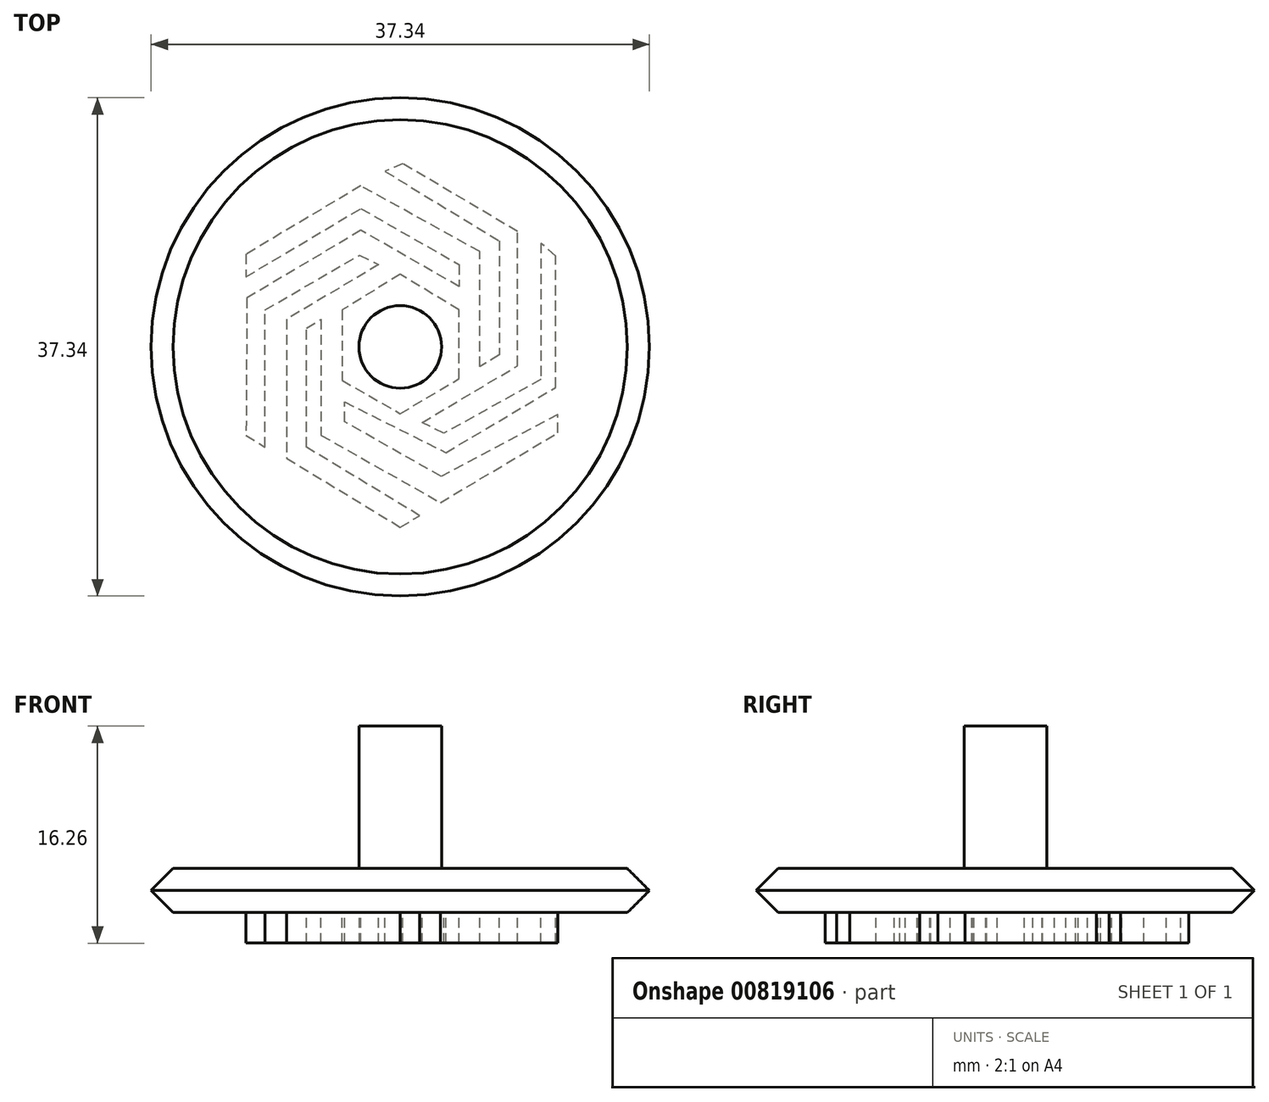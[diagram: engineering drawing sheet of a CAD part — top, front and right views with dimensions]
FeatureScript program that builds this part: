
annotation { "Feature Type Name" : "Feature", "Feature Type Description" : "" }
export const myFeature = defineFeature(function(context is Context, id is Id, definition is map)
    precondition{}
    {
        {
            var Q0;
            Q0=qCreatedBy(makeId("Top.planeOp"),FACE);
            var sketch = newSketch(context, id + "F0", { "sketchPlane" : qUnion([Q0])});
            skCircle(sketch, "E0", {"center": v(0, 0) * mm, "radius": 19.05 * mm});
            skSolve(sketch);
        }
        {
            var Q0;
            Q0=makeQuery(id+"F0.imprint","IMPRINT",FACE,{"disambiguationData":[TD([[makeQuery(id+"F0.imprint","IMPRINT",EDGE,{"derivedFrom":sQuery(id+"F0.wireOp",EDGE,"E0")}),1.0]])]});
            extrude(context, id + "F1", {"entities" : qUnion([Q0]), "depth" : 3.3 * mm, "offsetDistance" : 25.4 * mm});
        }
        {
            var Q0;
            Q0=makeQuery(id+"F1.opExtrude","CAP_FACE",FACE,{"disambiguationData":[OSD([sQuery(id+"F0.wireOp",EDGE,"E0")])],"isStart":false});
            var sketch = newSketch(context, id + "F2", { "sketchPlane" : qUnion([Q0])});
            skCircle(sketch, "E1", {"center": v(0, 0) * mm, "radius": 3.1 * mm});
            skSolve(sketch);
        }
        {
            var Q0;
            Q0=makeQuery(id+"F2.imprint","IMPRINT",FACE,{"disambiguationData":[TD([[makeQuery(id+"F2.imprint","IMPRINT",EDGE,{"derivedFrom":sQuery(id+"F2.wireOp",EDGE,"E1")}),1.0]])]});
            extrude(context, id + "F3", {"entities" : qUnion([Q0]), "operationType" : NewBodyOperationType.ADD, "depth" : 10.67 * mm, "offsetDistance" : 25.4 * mm});
        }
        {
            var Q0;
            Q0=makeQuery(id+"F1.opExtrude","CAP_EDGE",EDGE,{"disambiguationData":[OSD([sQuery(id+"F0.wireOp",EDGE,"E0")])],"isStart":false});
            chamfer(context, id + "F4", {"entities" : qUnion([Q0]), "width" : 2.03 * mm, "tangentPropagation" : true});
        }
        {
            var Q0;
            Q0=makeQuery(id+"F1.opExtrude","CAP_EDGE",EDGE,{"disambiguationData":[OSD([sQuery(id+"F0.wireOp",EDGE,"E0")])],"isStart":true});
            chamfer(context, id + "F5", {"entities" : qUnion([Q0]), "width" : 2.03 * mm, "tangentPropagation" : true});
        }
        {
            var Q0;
            Q0=makeQuery(id+"F1.opExtrude","CAP_FACE",FACE,{"disambiguationData":[OSD([sQuery(id+"F0.wireOp",EDGE,"E0")])],"isStart":true});
            var sketch = newSketch(context, id + "F6", { "sketchPlane" : qUnion([Q0])});
            skLineSegment(sketch, "E2", {"start": v(-11.55, 6.62) * mm, "end": v(-10.12, 7.5) * mm});
            skLineSegment(sketch, "E3", {"start": v(-10.12, 7.5) * mm, "end": v(-10.12, -2.78) * mm});
            skLineSegment(sketch, "E4", {"start": v(-10.12, -2.78) * mm, "end": v(-3.05, -6.88) * mm});
            skLineSegment(sketch, "E5", {"start": v(-3.05, -6.88) * mm, "end": v(-1.62, -6.16) * mm});
            skLineSegment(sketch, "E6", {"start": v(-1.62, -6.16) * mm, "end": v(-8.52, -2.06) * mm});
            skLineSegment(sketch, "E7", {"start": v(-8.52, -2.06) * mm, "end": v(-8.52, 8.34) * mm});
            skLineSegment(sketch, "E8", {"start": v(-8.52, 8.34) * mm, "end": v(0, 13.5) * mm});
            skLineSegment(sketch, "E9", {"start": v(0, 13.5) * mm, "end": v(1.45, 12.65) * mm});
            skLineSegment(sketch, "E10", {"start": v(1.45, 12.65) * mm, "end": v(-7.03, 7.5) * mm});
            skLineSegment(sketch, "E11", {"start": v(-7.03, 7.5) * mm, "end": v(-7.03, -1.4) * mm});
            skLineSegment(sketch, "E12", {"start": v(-7.03, -1.4) * mm, "end": v(-5.93, -2.06) * mm});
            skLineSegment(sketch, "E13", {"start": v(-5.93, -2.06) * mm, "end": v(-5.93, 6.62) * mm});
            skLineSegment(sketch, "E14", {"start": v(-5.93, 6.62) * mm, "end": v(3.01, 11.67) * mm});
            skLineSegment(sketch, "E15", {"start": v(3.01, 11.67) * mm, "end": v(11.82, 6.43) * mm});
            skLineSegment(sketch, "E16", {"start": v(11.82, 6.43) * mm, "end": v(11.82, 5.07) * mm});
            skLineSegment(sketch, "E17", {"start": v(11.82, 5.07) * mm, "end": v(3.07, 9.7) * mm});
            skLineSegment(sketch, "E18", {"start": v(3.07, 9.7) * mm, "end": v(-4.18, 5.6) * mm});
            skLineSegment(sketch, "E19", {"start": v(-4.18, 5.6) * mm, "end": v(-4.18, 4.12) * mm});
            skLineSegment(sketch, "E20", {"start": v(-4.18, 4.12) * mm, "end": v(3.43, 7.92) * mm});
            skLineSegment(sketch, "E21", {"start": v(3.43, 7.92) * mm, "end": v(11.65, 3.03) * mm});
            skLineSegment(sketch, "E22", {"start": v(11.65, 3.03) * mm, "end": v(11.65, -6.82) * mm});
            skLineSegment(sketch, "E23", {"start": v(11.65, -6.82) * mm, "end": v(10.54, -7.77) * mm});
            skLineSegment(sketch, "E24", {"start": v(10.54, -7.77) * mm, "end": v(10.54, 2.44) * mm});
            skLineSegment(sketch, "E25", {"start": v(10.54, 2.44) * mm, "end": v(3.27, 6.48) * mm});
            skLineSegment(sketch, "E26", {"start": v(3.27, 6.48) * mm, "end": v(1.64, 5.66) * mm});
            skLineSegment(sketch, "E27", {"start": v(1.64, 5.66) * mm, "end": v(8.8, 1.4) * mm});
            skLineSegment(sketch, "E28", {"start": v(8.8, 1.4) * mm, "end": v(8.8, -8.64) * mm});
            skLineSegment(sketch, "E29", {"start": v(8.8, -8.64) * mm, "end": v(0.19, -13.74) * mm});
            skLineSegment(sketch, "E30", {"start": v(0.19, -13.74) * mm, "end": v(-1.14, -13.15) * mm});
            skLineSegment(sketch, "E31", {"start": v(-1.14, -13.15) * mm, "end": v(7.41, -7.96) * mm});
            skLineSegment(sketch, "E32", {"start": v(7.41, -7.96) * mm, "end": v(7.41, 0.6) * mm});
            skLineSegment(sketch, "E33", {"start": v(7.41, 0.6) * mm, "end": v(5.96, 1.47) * mm});
            skLineSegment(sketch, "E34", {"start": v(5.96, 1.47) * mm, "end": v(5.96, -7.15) * mm});
            skLineSegment(sketch, "E35", {"start": v(5.96, -7.15) * mm, "end": v(-2.96, -12.06) * mm});
            skLineSegment(sketch, "E36", {"start": v(-2.96, -12.06) * mm, "end": v(-11.56, -6.95) * mm});
            skLineSegment(sketch, "E37", {"start": v(-11.56, -6.95) * mm, "end": v(-11.56, -5.26) * mm});
            skLineSegment(sketch, "E38", {"start": v(-11.56, -5.26) * mm, "end": v(-2.96, -10.37) * mm});
            skLineSegment(sketch, "E39", {"start": v(-2.96, -10.37) * mm, "end": v(4.42, -6.16) * mm});
            skLineSegment(sketch, "E40", {"start": v(4.42, -6.16) * mm, "end": v(4.42, -4.53) * mm});
            skLineSegment(sketch, "E41", {"start": v(4.42, -4.53) * mm, "end": v(-2.96, -8.74) * mm});
            skLineSegment(sketch, "E42", {"start": v(-2.96, -8.74) * mm, "end": v(-11.5, -3.66) * mm});
            skLineSegment(sketch, "E43", {"start": v(-11.5, -3.66) * mm, "end": v(-11.55, 6.62) * mm});
            skLineSegment(sketch, "E44", {"start": v(-4.36, -2.76) * mm, "end": v(-4.36, 2.51) * mm});
            skLineSegment(sketch, "E45", {"start": v(-4.36, 2.51) * mm, "end": v(0, 5) * mm});
            skLineSegment(sketch, "E46", {"start": v(0, 5) * mm, "end": v(4.42, 2.37) * mm});
            skLineSegment(sketch, "E47", {"start": v(4.42, 2.37) * mm, "end": v(4.42, -2.76) * mm});
            skLineSegment(sketch, "E48", {"start": v(4.42, -2.76) * mm, "end": v(0, -5.45) * mm});
            skLineSegment(sketch, "E49", {"start": v(0, -5.45) * mm, "end": v(-4.36, -2.76) * mm});
            skSolve(sketch);
        }
        {
            var Q0;
            Q0 = qSketchRegion(id + "F6", true);
            extrude(context, id + "F7", {"entities" : qUnion([Q0]), "operationType" : NewBodyOperationType.ADD, "depth" : 2.3 * mm, "offsetDistance" : 25.4 * mm});
        }
    });
